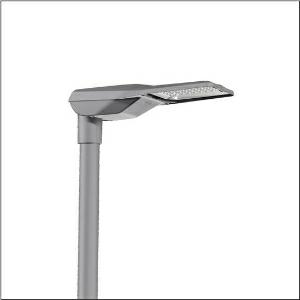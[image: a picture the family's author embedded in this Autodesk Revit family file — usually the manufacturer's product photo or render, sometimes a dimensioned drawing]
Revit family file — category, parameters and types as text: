
# Revit family: streetlight_sl_21_iq_mini___st1_0ab_5xe2m31d08hb_2a38
name_source: partatom
category: Lighting Fixtures
units: mm (PartAtom-declared; Revit-internal decimal feet)

## family parameters
Cut with Voids When Loaded = No
Host = Face
Light Source = No
Part Type = Normal
Room Calculation Point = No
Round Connector Dimension = Use Diameter
Shared = No

## types (1)
- --- (1 x LED, 8320 lm, 70.9 W, 3000K)
    Apparent Load = 71 VA
    CIE Flux Codes = 38 73 97 100 100
    Color Rendering = 70
    Color Temperature = 3000K
    Default Elevation = 1800 mm
    Description = Streetlight SL 21 iQ mini, mast luminaire, primary light control with lens, of PMMA, primary optical cover: cover, of toughened safety glass, transparent, light distribution: ST1.0aB, light emission: direct distribution, primary light characteristic: asymmetric, installation type: post-top, side-entry, LED, High Power LED, rated luminous flux: 8.320lm, luminous efficacy: 117lm/W, light colour: 730, colour temperature: 3000K, control gear: iQ-Comfort, control: Auto-Match, Temp-Guard, Lumen-Switch, Night-Set, Smart-Wire, Light-Fading, Desk-Remote (wireless, voltage-free reading and setting of iQ features in the workshop via application-optimized NFC function/RFID function), optimised constant luminous flux control (CLO 2.0), pre-setting: linear dimming characteristic, mains connection: 220..240V, AC, 50/60Hz, start of lifetime: 71W, end of service life: 75W, reduction: 31W, luminaire housing, of diecast aluminium, powder-coated, Siteco® metallic grey (DB 702S), corrosivity category C5 mid according to DIN EN ISO 12944, please order mast flange separately, inclination adjustable: 0°, 5°, 10°, 15°, sealing non-destructively replaceable, multi-level sealing system, length: 628mm, width: 235mm, height: 110mm, mast flange for spigot size: 42mm (side-entry): 5XC10008XM4, 60/48mm (side-entry/post-top): 5XC10108XM2, 76/60mm (side-entry/post-top): 5XC10108XM1, mounting height: 4..8m, protection rating (complete): IP66, insulation class (complete): insulation class II (safety insulation), certification: CE, ENEC, ENEC+, VDE, impact resistance: IK10, permissible operating ambient temperature for outdoor applications: -40..+50°C, standard-compliant lighting for roads and squares, packaging unit: 1 piece

Light Distribution: ST1.0aB
    Height = 110 mm
    Lamp = 1 x LED
    Lamp Light Flux = 8320 lm
    Lamp Power = 70.9 W
    Lamp count = 1
    Length = 625 mm
    Luminous efficacy = 117 lm/W
    Manufacturer = Siteco
    ModVariant = No
    Model = 5XE2M31D08HB
    Number of Poles = 1
    OnlyDefault = Yes
    Power Factor = 1
    Product Name = Streetlight SL 21 iQ mini | ST1.0aB
    Product group = mast luminaire | pylon top
    ProductGroupID = 6100
    Protection Class = Protection class II
    Protection Degree = IP 66
    RLX_Detail_Level = 1
    RLX_Emergency_Light_Flux = 0 lm
    RLX_Emergency_Type = 0
    RLX_Emergency_Type_DB = No
    RlxData = <blob elided: 26321 chars, md5=87810ffa>
    Socket = socket
    Standby Power = 0 W
    System Light Flux = 8320 lm
    System Power = 71 W
    Type Comments = factory setting: luminous flux: 100 % | dim-lin: 254 | 711 mA
    Type Image = l_1003519.jpg
    URL = http://relux.com
    VarID = @adj_178641
    Voltage = 0 V
    Weight = 0.00 kg
    Width = 234 mm

## geometry (parser evidence)
native form markers: Blend x4, Sweep x10
no freeform markers — native parametric forms only
